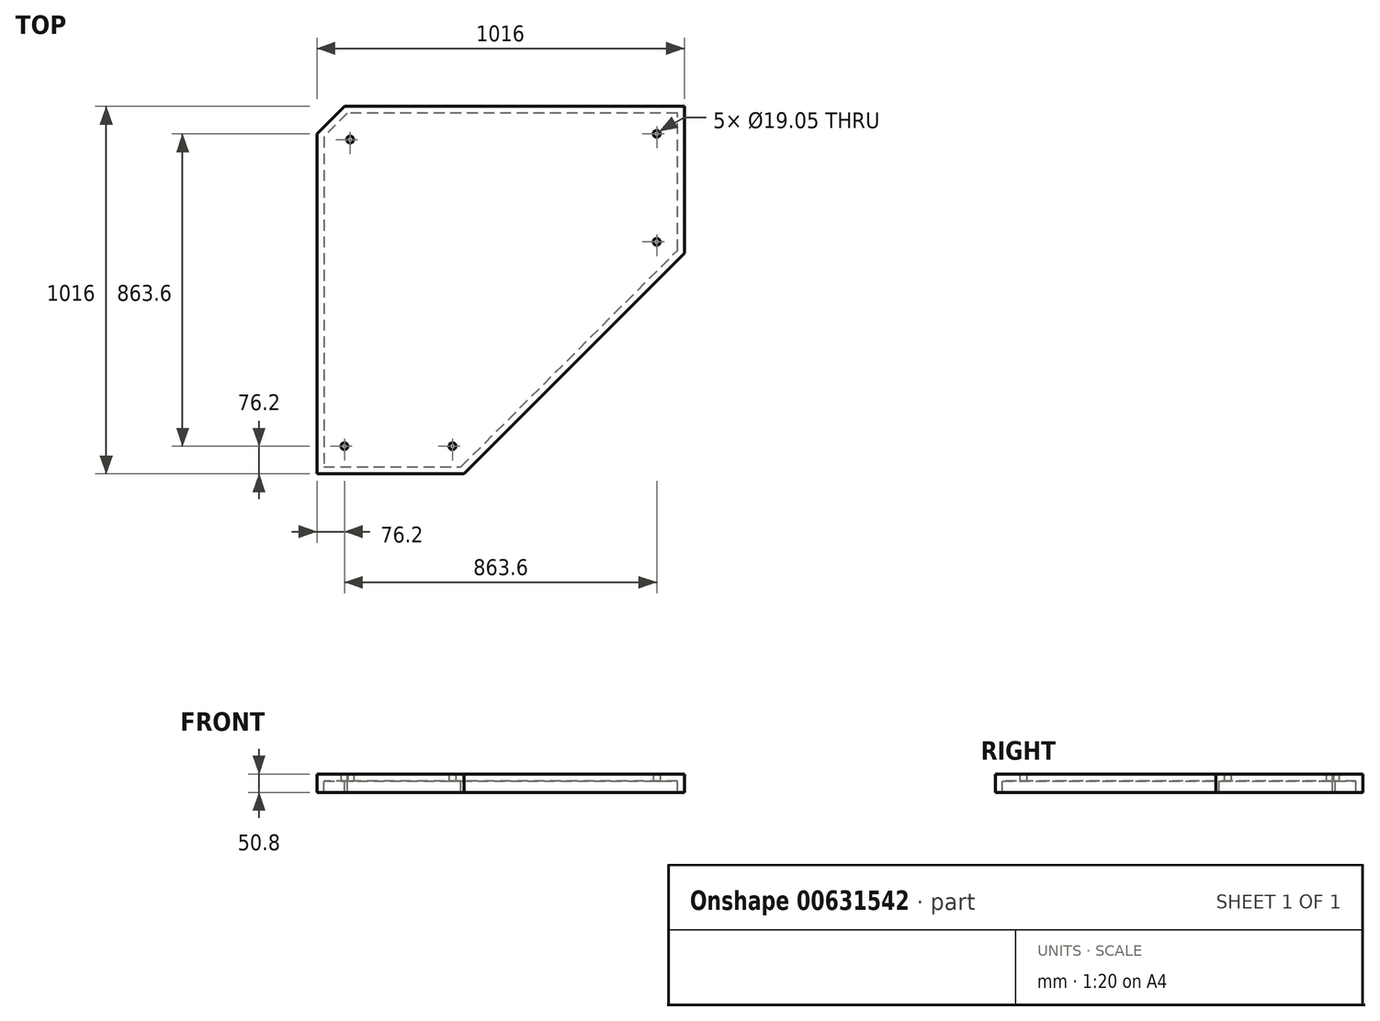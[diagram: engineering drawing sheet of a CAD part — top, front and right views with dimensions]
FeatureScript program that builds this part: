
annotation { "Feature Type Name" : "Feature", "Feature Type Description" : "" }
export const myFeature = defineFeature(function(context is Context, id is Id, definition is map)
    precondition{}
    {
        {
            var Q0;
            Q0=qCreatedBy(makeId("Top.planeOp"),FACE);
            var sketch = newSketch(context, id + "F0", { "sketchPlane" : qUnion([Q0])});
            skLineSegment(sketch, "E0", {"start": v(0, -1016) * mm, "end": v(406.4, -1016) * mm});
            skLineSegment(sketch, "E1", {"start": v(406.4, -1016) * mm, "end": v(1016, -406.4) * mm});
            skLineSegment(sketch, "E2", {"start": v(1016, -406.4) * mm, "end": v(1016, 0) * mm});
            skLineSegment(sketch, "E3", {"start": v(1016, 0) * mm, "end": v(76.2, 0) * mm});
            skLineSegment(sketch, "E4", {"start": v(76.2, 0) * mm, "end": v(0, -76.2) * mm});
            skLineSegment(sketch, "E5", {"start": v(0, -76.2) * mm, "end": v(0, -1016) * mm});
            skLineSegment(sketch, "E6.0", {"start": v(19.05, -996.95) * mm, "end": v(398.5, -996.95) * mm});
            skLineSegment(sketch, "E6.1", {"start": v(996.95, -398.5) * mm, "end": v(996.95, -19.05) * mm});
            skLineSegment(sketch, "E6.2", {"start": v(996.95, -19.05) * mm, "end": v(84.1, -19.05) * mm});
            skLineSegment(sketch, "E6.3", {"start": v(398.5, -996.95) * mm, "end": v(996.95, -398.5) * mm});
            skLineSegment(sketch, "E6.4", {"start": v(84.1, -19.05) * mm, "end": v(19.05, -84.1) * mm});
            skLineSegment(sketch, "E6.5", {"start": v(19.05, -84.1) * mm, "end": v(19.05, -996.95) * mm});
            skSolve(sketch);
        }
        {
            var Q0;
            Q0=qSketchRegion(id+"F0",true);
            extrude(context, id + "F1", {"entities" : qUnion([Q0]), "oppositeDirection" : true, "depth" : 50.8 * mm, "offsetDistance" : 25.4 * mm});
        }
        {
            var Q0;
            Q0=makeQuery(id+"F0.imprint","IMPRINT",FACE,{"disambiguationData":[TD([[makeQuery(id+"F0.imprint","IMPRINT",EDGE,{"derivedFrom":sQuery(id+"F0.wireOp",EDGE,"E6.0")}),1.0]])]});
            extrude(context, id + "F2", {"entities" : qUnion([Q0]), "operationType" : NewBodyOperationType.ADD, "oppositeDirection" : true, "depth" : 19.05 * mm, "offsetDistance" : 25.4 * mm});
        }
        {
            var Q0;
            Q0=makeQuery(id+"F2.opExtrude","CAP_FACE",FACE,{"disambiguationData":[OSD([sQuery(id+"F0.wireOp",EDGE,"E6.0"),sQuery(id+"F0.wireOp",EDGE,"E6.1"),sQuery(id+"F0.wireOp",EDGE,"E6.2"),sQuery(id+"F0.wireOp",EDGE,"E6.3"),sQuery(id+"F0.wireOp",EDGE,"E6.4"),sQuery(id+"F0.wireOp",EDGE,"E6.5")])],"isStart":false});
            var sketch = newSketch(context, id + "F3", { "sketchPlane" : qUnion([Q0])});
            skLineSegment(sketch, "E7.0", {"start": v(939.8, 76.2) * mm, "end": v(107.76, 76.2) * mm, "construction": true});
            skLineSegment(sketch, "E7.1", {"start": v(76.2, 107.76) * mm, "end": v(76.2, 939.8) * mm, "construction": true});
            skLineSegment(sketch, "E7.2", {"start": v(76.2, 939.8) * mm, "end": v(374.84, 939.8) * mm, "construction": true});
            skLineSegment(sketch, "E7.3", {"start": v(107.76, 76.2) * mm, "end": v(76.2, 107.76) * mm, "construction": true});
            skLineSegment(sketch, "E7.4", {"start": v(374.84, 939.8) * mm, "end": v(939.8, 374.84) * mm, "construction": true});
            skLineSegment(sketch, "E7.5", {"start": v(939.8, 374.84) * mm, "end": v(939.8, 76.2) * mm, "construction": true});
            skCircle(sketch, "E8", {"center": v(76.2, 939.8) * mm, "radius": 9.52 * mm});
            skCircle(sketch, "E9", {"center": v(91.98, 91.98) * mm, "radius": 9.52 * mm});
            skCircle(sketch, "E10", {"center": v(374.84, 939.8) * mm, "radius": 9.52 * mm});
            skCircle(sketch, "E11", {"center": v(939.8, 374.84) * mm, "radius": 9.52 * mm});
            skCircle(sketch, "E12", {"center": v(939.8, 76.2) * mm, "radius": 9.52 * mm});
            skSolve(sketch);
        }
        {
            var Q0;
            Q0 = qSketchRegion(id + "F3", true);
            extrude(context, id + "F4", {"entities" : qUnion([Q0]), "operationType" : NewBodyOperationType.REMOVE, "endBound" : BoundingType.UP_TO_NEXT, "oppositeDirection" : true, "depth" : 25.4 * mm, "offsetDistance" : 25.4 * mm});
        }
    });
